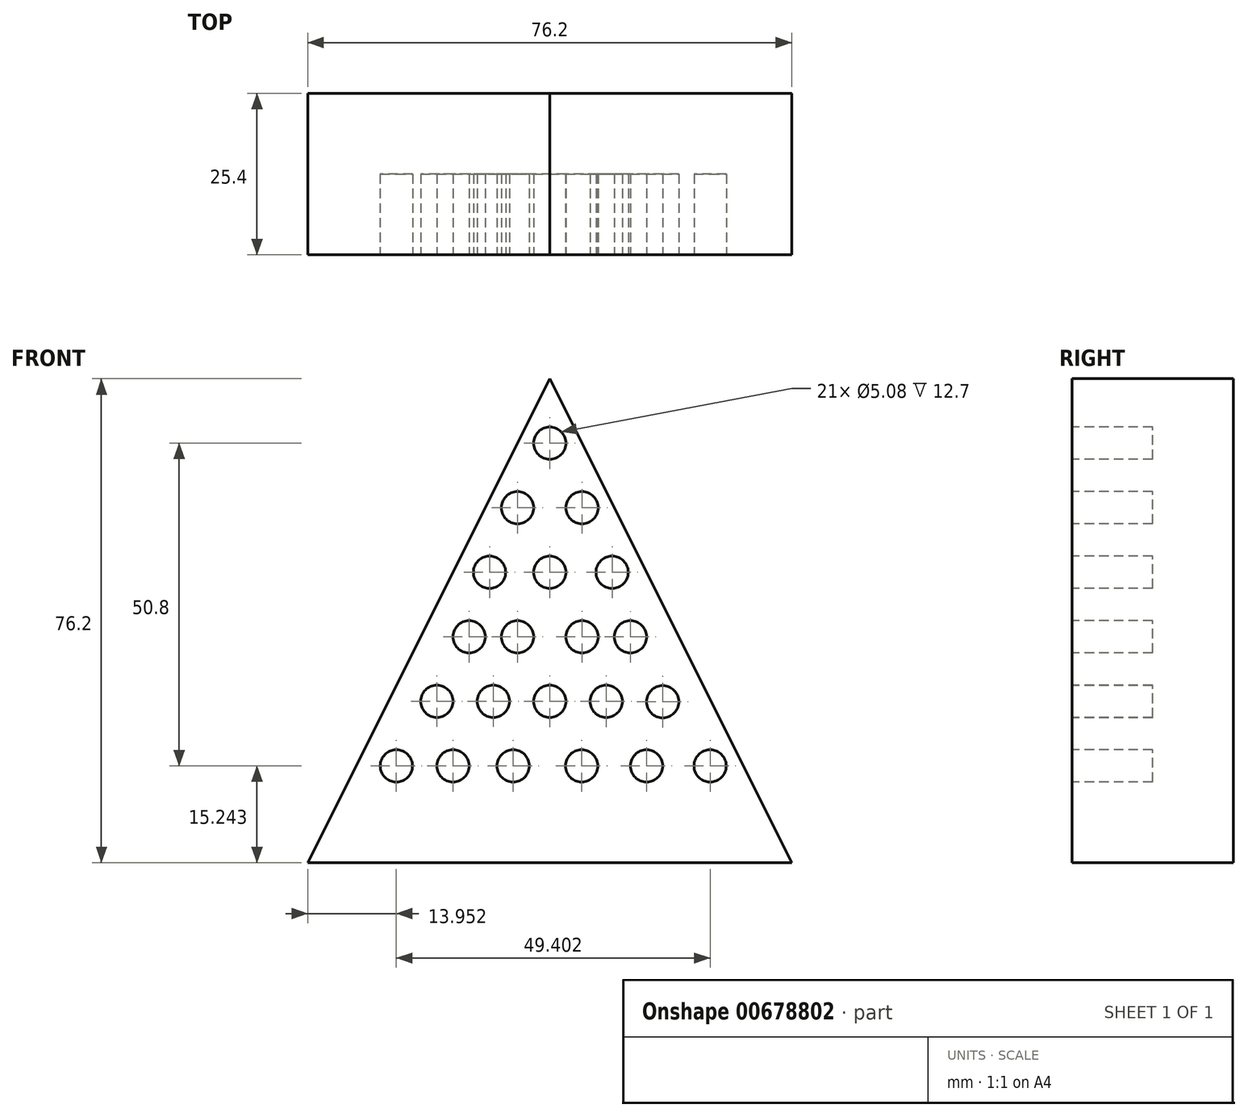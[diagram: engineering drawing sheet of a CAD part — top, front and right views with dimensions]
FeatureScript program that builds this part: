
annotation { "Feature Type Name" : "Feature", "Feature Type Description" : "" }
export const myFeature = defineFeature(function(context is Context, id is Id, definition is map)
    precondition{}
    {
        {
            var Q0;
            Q0=qCreatedBy(makeId("Front.planeOp"),FACE);
            var sketch = newSketch(context, id + "F0", { "sketchPlane" : qUnion([Q0])});
            skLineSegment(sketch, "E0.top", {"start": v(-32.35, -39.8) * mm, "end": v(43.85, -39.8) * mm});
            skLineSegment(sketch, "E0.left", {"start": v(-32.35, 0) * mm, "end": v(-32.35, -1.7) * mm});
            skPoint(sketch, "E1.startSnap0", {"position": v(-32.35, -1.7) * mm});
            skLineSegment(sketch, "E2", {"start": v(5.75, 36.4) * mm, "end": v(-32.35, -39.8) * mm});
            skLineSegment(sketch, "E3", {"start": v(5.75, 36.4) * mm, "end": v(43.85, -39.8) * mm});
            skPoint(sketch, "E4.orphan", {"position": v(-32.35, 36.4) * mm});
            skPoint(sketch, "E0.right.start.orphan", {"position": v(43.85, 36.4) * mm});
            skLineSegment(sketch, "E5", {"start": v(5.75, 36.4) * mm, "end": v(5.75, -39.8) * mm});
            skLineSegment(sketch, "E6", {"start": v(5.75, 36.4) * mm, "end": v(5.75, 34.85) * mm});
            skSolve(sketch);
        }
        {
            var Q0;
            Q0 = qSketchRegion(id + "F0", true);
            extrude(context, id + "F1", {"entities" : qUnion([Q0]), "depth" : 25.4 * mm, "offsetDistance" : 25.4 * mm});
        }
        {
            var Q0;
            Q0=makeQuery(id+"F1.opExtrude","CAP_FACE",FACE,{"disambiguationData":[OSD([sQuery(id+"F0.wireOp",EDGE,"E0.top"),sQuery(id+"F0.wireOp",EDGE,"E2"),sQuery(id+"F0.wireOp",EDGE,"E3")])],"isStart":false});
            var sketch = newSketch(context, id + "F2", { "sketchPlane" : qUnion([Q0])});
            skLineSegment(sketch, "E7", {"start": v(5.75, 36.4) * mm, "end": v(5.75, 26.24) * mm});
            skCircle(sketch, "E8", {"center": v(5.75, 26.24) * mm, "radius": 2.54 * mm});
            skLineSegment(sketch, "E9", {"start": v(5.75, 26.24) * mm, "end": v(5.75, 16.08) * mm});
            skCircle(sketch, "E10", {"center": v(0.67, 16.08) * mm, "radius": 2.54 * mm});
            skCircle(sketch, "E11", {"center": v(10.83, 16.08) * mm, "radius": 2.54 * mm});
            skLineSegment(sketch, "E12", {"start": v(5.75, 16.08) * mm, "end": v(5.75, 5.92) * mm});
            skCircle(sketch, "E13", {"center": v(5.75, 5.92) * mm, "radius": 2.54 * mm});
            skLineSegment(sketch, "E14", {"start": v(-1.19, 5.92) * mm, "end": v(-1.87, 5.92) * mm});
            skCircle(sketch, "E15", {"center": v(-3.73, 5.92) * mm, "radius": 2.54 * mm});
            skCircle(sketch, "E16", {"center": v(15.58, 5.92) * mm, "radius": 2.54 * mm});
            skLineSegment(sketch, "E17", {"start": v(5.75, 5.92) * mm, "end": v(5.75, -4.24) * mm});
            skLineSegment(sketch, "E18", {"start": v(5.75, -4.24) * mm, "end": v(5.75, -14.4) * mm});
            skLineSegment(sketch, "E19", {"start": v(5.75, -14.4) * mm, "end": v(5.75, -24.56) * mm});
            skLineSegment(sketch, "E20", {"start": v(5.75, -24.56) * mm, "end": v(5.75, -34.72) * mm});
            skPoint(sketch, "E20.endSnap0", {"position": v(5.75, -39.8) * mm});
            skLineSegment(sketch, "E21", {"start": v(5.75, -34.72) * mm, "end": v(5.75, -39.8) * mm});
            skPoint(sketch, "E22.orphan", {"position": v(-14.57, -4.24) * mm});
            skCircle(sketch, "E23", {"center": v(0.67, -4.24) * mm, "radius": 2.54 * mm});
            skCircle(sketch, "E24", {"center": v(-6.95, -4.24) * mm, "radius": 2.54 * mm});
            skCircle(sketch, "E25", {"center": v(10.83, -4.24) * mm, "radius": 2.54 * mm});
            skCircle(sketch, "E26", {"center": v(18.45, -4.25) * mm, "radius": 2.54 * mm});
            skCircle(sketch, "E27", {"center": v(5.75, -14.4) * mm, "radius": 2.54 * mm});
            skPoint(sketch, "E28.start.orphan", {"position": v(-1.87, -4.24) * mm});
            skLineSegment(sketch, "E29.trimOffspring", {"start": v(13.04, 5.92) * mm, "end": v(13.37, 5.92) * mm});
            skCircle(sketch, "E30", {"center": v(-3.14, -14.38) * mm, "radius": 2.54 * mm});
            skCircle(sketch, "E31", {"center": v(-12.03, -14.38) * mm, "radius": 2.54 * mm});
            skLineSegment(sketch, "E32", {"start": v(12.1, -14.4) * mm, "end": v(14.64, -14.4) * mm});
            skCircle(sketch, "E33", {"center": v(14.64, -14.4) * mm, "radius": 2.54 * mm});
            skLineSegment(sketch, "E34", {"start": v(20.99, -14.46) * mm, "end": v(23.53, -14.46) * mm});
            skCircle(sketch, "E35", {"center": v(23.53, -14.46) * mm, "radius": 2.54 * mm});
            skPoint(sketch, "E36.orphan", {"position": v(-5.68, -14.38) * mm});
            skPoint(sketch, "E37.orphan", {"position": v(8.29, -14.4) * mm});
            skPoint(sketch, "E38.orphan", {"position": v(-24.73, -24.56) * mm});
            skCircle(sketch, "E39", {"center": v(0, -24.56) * mm, "radius": 2.54 * mm});
            skCircle(sketch, "E40", {"center": v(-9.5, -24.56) * mm, "radius": 2.54 * mm});
            skCircle(sketch, "E41", {"center": v(-18.4, -24.56) * mm, "radius": 2.54 * mm});
            skCircle(sketch, "E42", {"center": v(10.77, -24.56) * mm, "radius": 2.54 * mm});
            skCircle(sketch, "E43", {"center": v(20.99, -24.56) * mm, "radius": 2.54 * mm});
            skCircle(sketch, "E44", {"center": v(31, -24.56) * mm, "radius": 2.54 * mm});
            skSolve(sketch);
        }
        {
            var Q0;
            Q0 = qSketchRegion(id + "F2", true);
            extrude(context, id + "F3", {"entities" : qUnion([Q0]), "operationType" : NewBodyOperationType.REMOVE, "oppositeDirection" : true, "depth" : 12.7 * mm, "offsetDistance" : 25.4 * mm});
        }
    });
